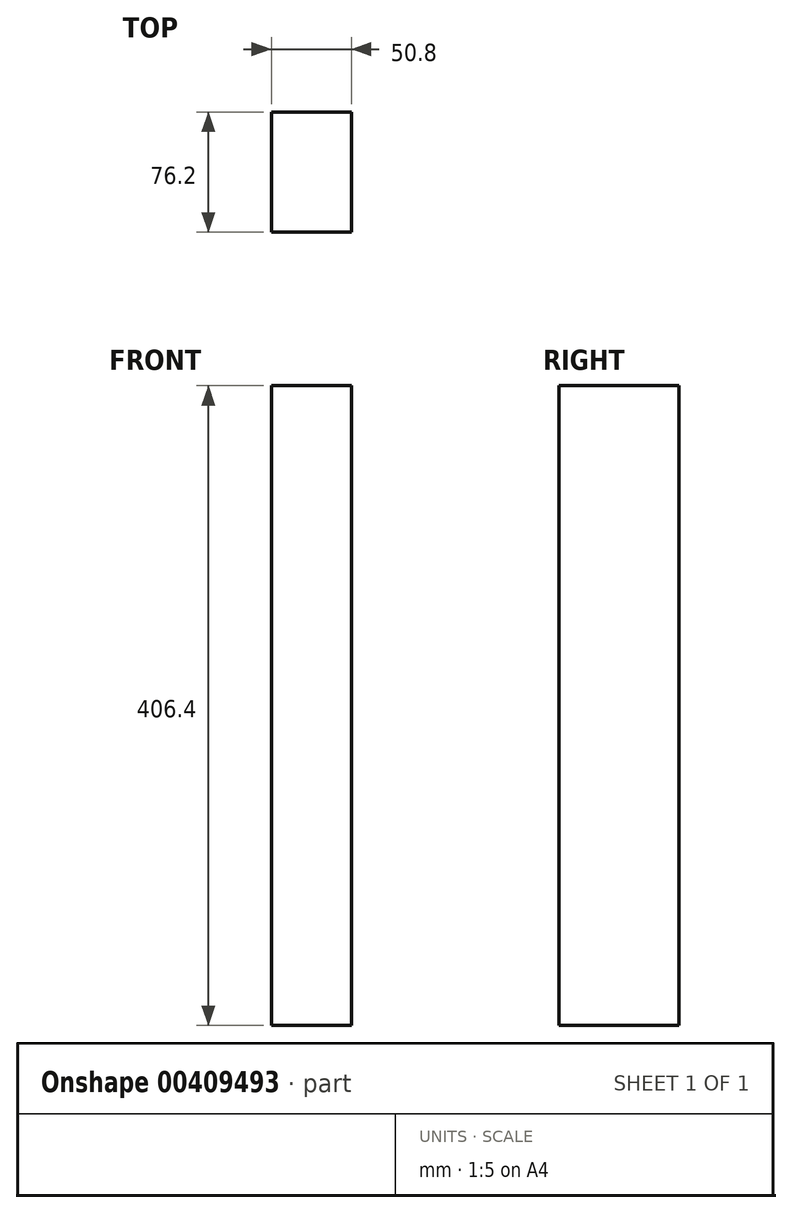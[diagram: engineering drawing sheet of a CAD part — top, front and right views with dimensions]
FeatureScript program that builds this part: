
annotation { "Feature Type Name" : "Feature", "Feature Type Description" : "" }
export const myFeature = defineFeature(function(context is Context, id is Id, definition is map)
    precondition{}
    {
        {
            var Q0;
            Q0=qCreatedBy(makeId("Front.planeOp"),FACE);
            var sketch = newSketch(context, id + "F0", { "sketchPlane" : qUnion([Q0])});
            skLineSegment(sketch, "E0.bottom", {"start": v(-25.4, 203.2) * mm, "end": v(25.4, 203.2) * mm});
            skLineSegment(sketch, "E0.top", {"start": v(-25.4, -203.2) * mm, "end": v(25.4, -203.2) * mm});
            skLineSegment(sketch, "E0.left", {"start": v(-25.4, 203.2) * mm, "end": v(-25.4, -203.2) * mm});
            skLineSegment(sketch, "E0.right", {"start": v(25.4, 203.2) * mm, "end": v(25.4, -203.2) * mm});
            skSolve(sketch);
        }
        {
            var Q0;
            Q0=makeQuery(id+"F0.imprint","IMPRINT",FACE,{"disambiguationData":[TD([[makeQuery(id+"F0.imprint","IMPRINT",EDGE,{"derivedFrom":sQuery(id+"F0.wireOp",EDGE,"E0.bottom")}),-1.0]])]});
            extrude(context, id + "F1", {"entities" : qUnion([Q0]), "depth" : 76.2 * mm});
        }
    });
